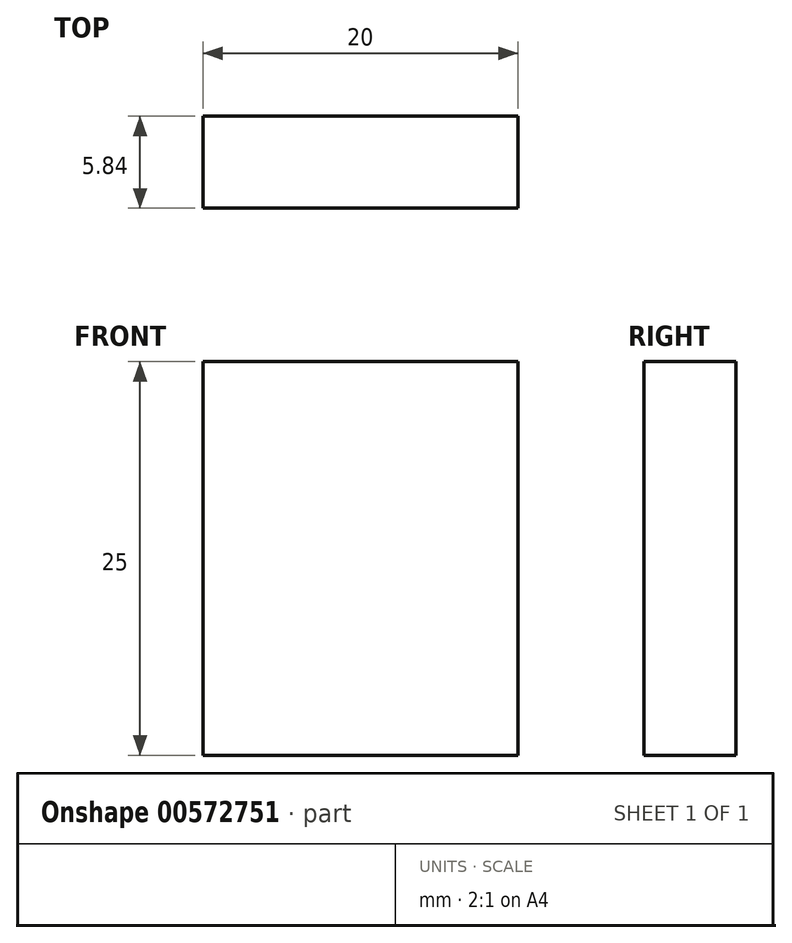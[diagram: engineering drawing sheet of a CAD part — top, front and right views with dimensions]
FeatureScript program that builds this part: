
annotation { "Feature Type Name" : "Feature", "Feature Type Description" : "" }
export const myFeature = defineFeature(function(context is Context, id is Id, definition is map)
    precondition{}
    {
        {
            var Q0;
            Q0=qCreatedBy(makeId("Front.planeOp"),FACE);
            var sketch = newSketch(context, id + "F0", { "sketchPlane" : qUnion([Q0])});
            skLineSegment(sketch, "E0.bottom", {"start": v(-6.64, 9.42) * mm, "end": v(13.36, 9.42) * mm});
            skLineSegment(sketch, "E0.top", {"start": v(-6.64, -15.58) * mm, "end": v(13.36, -15.58) * mm});
            skLineSegment(sketch, "E0.left", {"start": v(-6.64, 9.42) * mm, "end": v(-6.64, -15.58) * mm});
            skLineSegment(sketch, "E0.right", {"start": v(13.36, 9.42) * mm, "end": v(13.36, -15.58) * mm});
            skSolve(sketch);
        }
        {
            var Q0;
            Q0=makeQuery(id+"F0.imprint","IMPRINT",FACE,{"disambiguationData":[TD([[makeQuery(id+"F0.imprint","IMPRINT",EDGE,{"derivedFrom":sQuery(id+"F0.wireOp",EDGE,"E0.bottom")}),-1.0]])]});
            extrude(context, id + "F1", {"entities" : qUnion([Q0]), "depth" : 5.84 * mm, "offsetDistance" : 25.4 * mm});
        }
    });
